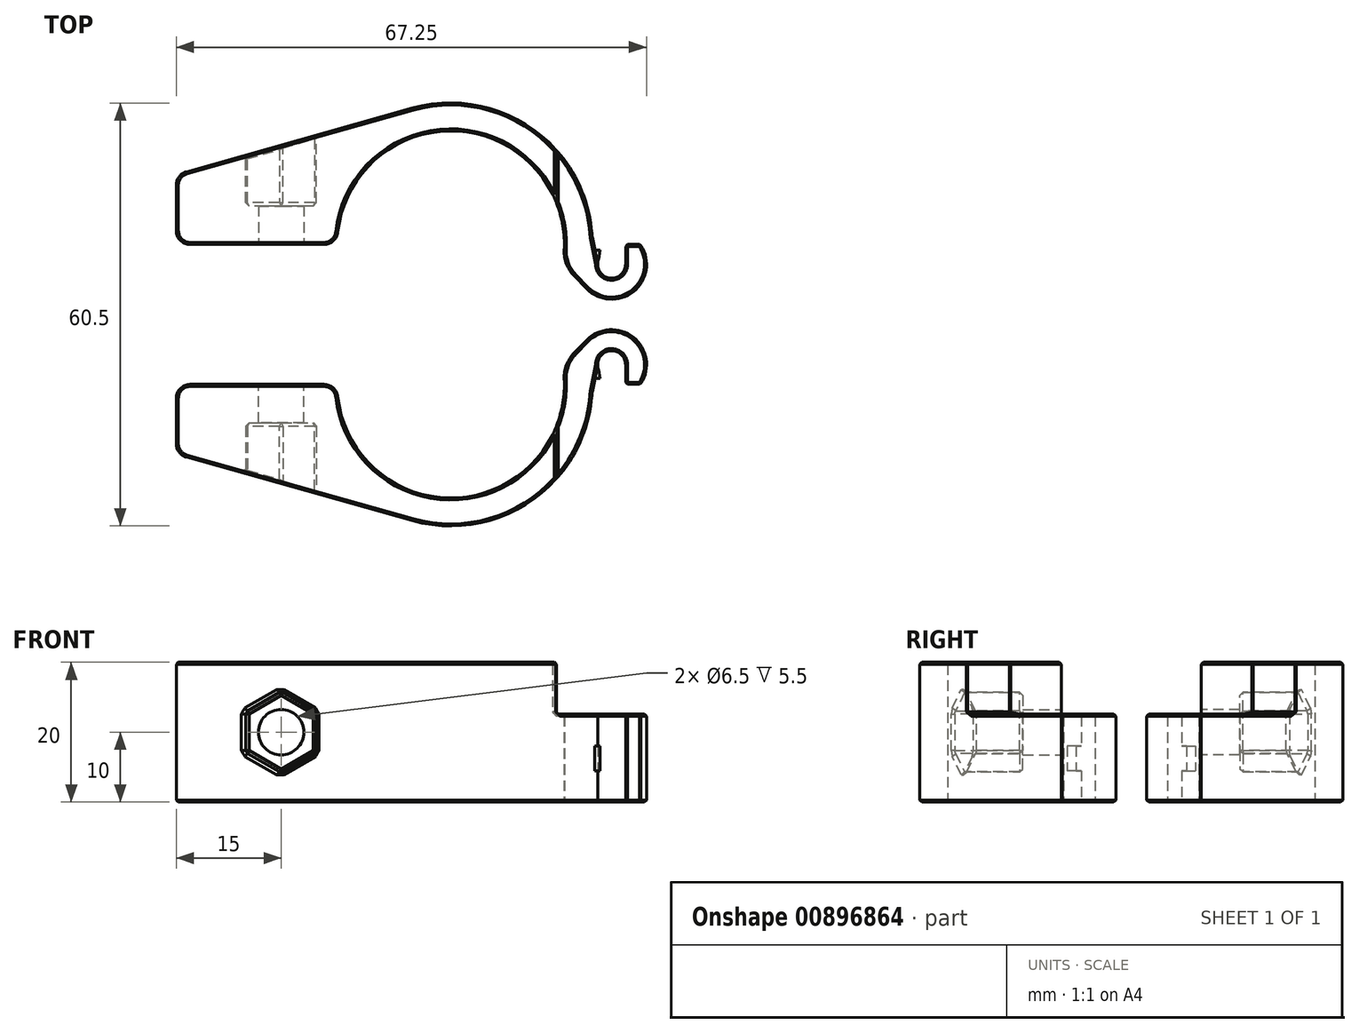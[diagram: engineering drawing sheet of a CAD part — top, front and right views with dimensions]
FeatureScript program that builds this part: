
annotation { "Feature Type Name" : "Feature", "Feature Type Description" : "" }
export const myFeature = defineFeature(function(context is Context, id is Id, definition is map)
    precondition{}
    {
        {
            var Q0;
            Q0=qCreatedBy(makeId("Top.planeOp"),FACE);
            var sketch = newSketch(context, id + "F0", { "sketchPlane" : qUnion([Q0])});
            skLineSegment(sketch, "E0", {"start": v(0, 0) * mm, "end": v(-16.25, 0) * mm, "construction": true});
            skLineSegment(sketch, "E1", {"start": v(0, 0) * mm, "end": v(16.25, 0) * mm, "construction": true});
            skLineSegment(sketch, "E2", {"start": v(0, 0) * mm, "end": v(16, -2.82) * mm, "construction": true});
            skArc(sketch, "E3", {"start": v(-16.25, 0) * mm, "mid": v(-1.42, -16.19) * mm, "end": v(16, -2.82) * mm, "construction": true});
            skArc(sketch, "E4", {"start": v(16, -2.82) * mm, "mid": v(1.42, 16.19) * mm, "end": v(-16.25, 0) * mm});
            skArc(sketch, "E5.0", {"start": v(19.94, -3.52) * mm, "mid": v(20.22, -1.1) * mm, "end": v(20.2, 1.32) * mm, "construction": true});
            skLineSegment(sketch, "E6", {"start": v(16, -2.82) * mm, "end": v(19.94, -3.52) * mm, "construction": true});
            skLineSegment(sketch, "E7", {"start": v(-16.25, 0) * mm, "end": v(-39.25, 0) * mm});
            skLineSegment(sketch, "E8", {"start": v(-39.25, 0) * mm, "end": v(-39.25, 10) * mm});
            skLineSegment(sketch, "E9", {"start": v(-39.25, 10) * mm, "end": v(-5.48, 19.5) * mm});
            skArc(sketch, "E10", {"start": v(-5.48, 19.5) * mm, "mid": v(-16.14, 12.23) * mm, "end": v(-20.25, 0) * mm, "construction": true});
            skArc(sketch, "E11", {"start": v(20.2, 1.32) * mm, "mid": v(11.7, 16.53) * mm, "end": v(-5.48, 19.5) * mm});
            skArc(sketch, "E12", {"start": v(20.2, 1.32) * mm, "mid": v(18.5, -0.63) * mm, "end": v(18.02, -3.18) * mm, "construction": true});
            skArc(sketch, "E13", {"start": v(18.02, -3.18) * mm, "mid": v(24.65, -7.54) * mm, "end": v(27.13, 0) * mm});
            skLineSegment(sketch, "E14", {"start": v(16, -2.82) * mm, "end": v(19.43, -6.32) * mm});
            skLineSegment(sketch, "E15", {"start": v(23, -2.82) * mm, "end": v(25, -2.82) * mm, "construction": true});
            skLineSegment(sketch, "E16", {"start": v(25, -2.82) * mm, "end": v(25, 0) * mm});
            skLineSegment(sketch, "E17", {"start": v(27.13, 0) * mm, "end": v(25, 0) * mm});
            skLineSegment(sketch, "E18", {"start": v(25, 0) * mm, "end": v(25, 1.76) * mm, "construction": true});
            skLineSegment(sketch, "E19", {"start": v(23, -2.82) * mm, "end": v(21, -2.82) * mm, "construction": true});
            skLineSegment(sketch, "E20", {"start": v(21, -2.82) * mm, "end": v(21, -2.82) * mm});
            skArc(sketch, "E21", {"start": v(27.13, 0) * mm, "mid": v(23.94, 2.09) * mm, "end": v(20.2, 1.32) * mm, "construction": true});
            skLineSegment(sketch, "E22", {"start": v(21, -2.82) * mm, "end": v(20.2, 1.32) * mm});
            skArc(sketch, "E23", {"start": v(21, -2.82) * mm, "mid": v(23, -4.82) * mm, "end": v(25, -2.82) * mm});
            skArc(sketch, "E24", {"start": v(25, -2.82) * mm, "mid": v(23, -0.82) * mm, "end": v(21, -2.82) * mm});
            skLineSegment(sketch, "E25", {"start": v(21, -2.82) * mm, "end": v(21, -0.82) * mm, "construction": true});
            skLineSegment(sketch, "E26", {"start": v(21, -2.82) * mm, "end": v(21.38, -0.82) * mm});
            skLineSegment(sketch, "E27", {"start": v(21.38, -0.82) * mm, "end": v(20.62, -0.82) * mm});
            skSolve(sketch);
        }
        {
            var Q0;
            Q0=makeQuery(id+"F0.imprint","IMPRINT",FACE,{"disambiguationData":[TD([[makeQuery(id+"F0.imprint","IMPRINT",EDGE,{"derivedFrom":sQuery(id+"F0.wireOp",EDGE,"E4")}),-1.0]])]});
            extrude(context, id + "F1", {"entities" : qUnion([Q0]), "depth" : 12.6 * mm, "offsetDistance" : 25 * mm});
        }
        {
            var Q0;
            Q0=makeQuery(id+"F1.opExtrude","CAP_FACE",FACE,{"disambiguationData":[OSD([sQuery(id+"F0.wireOp",EDGE,"E4"),sQuery(id+"F0.wireOp",EDGE,"E7"),sQuery(id+"F0.wireOp",EDGE,"E8"),sQuery(id+"F0.wireOp",EDGE,"E9"),sQuery(id+"F0.wireOp",EDGE,"E11"),sQuery(id+"F0.wireOp",EDGE,"E13"),sQuery(id+"F0.wireOp",EDGE,"E14"),sQuery(id+"F0.wireOp",EDGE,"E16"),sQuery(id+"F0.wireOp",EDGE,"E17"),sQuery(id+"F0.wireOp",EDGE,"E22"),sQuery(id+"F0.wireOp",EDGE,"E23")])],"isStart":false});
            var sketch = newSketch(context, id + "F2", { "sketchPlane" : qUnion([Q0])});
            skPoint(sketch, "E28.0", {"position": v(16.25, 0) * mm});
            skLineSegment(sketch, "E29", {"start": v(16.25, 0) * mm, "end": v(16.25, 6) * mm, "construction": true});
            skLineSegment(sketch, "E30", {"start": v(16.25, 6) * mm, "end": v(15.1, 6) * mm, "construction": true});
            skLineSegment(sketch, "E31", {"start": v(15.1, 6) * mm, "end": v(15.1, 13.5) * mm});
            skSolve(sketch);
        }
        {
            var Q0;
            {var subQ3=sQuery(id+"F2.wireOp",EDGE,"E31");Q0=makeQuery(id+"F2.imprint","IMPRINT",FACE,{"disambiguationData":[TD([[makeQuery(id+"F2.imprint","IMPRINT",EDGE,{"derivedFrom":subQ3}),1.0]])]});}
            extrude(context, id + "F3", {"entities" : qUnion([Q0]), "operationType" : NewBodyOperationType.ADD, "depth" : (20 - 12.6) * mm, "offsetDistance" : 25 * mm});
        }
        {
            var Q0;
            {var subQ0=sQuery(id+"F0.wireOp",EDGE,"E7");Q0=makeQuery(id+"F3.boolean.opBoolean","MERGE",FACE,{"derivedFrom":[makeQuery(id+"F1.opExtrude","SWEPT_FACE",FACE,{"disambiguationData":[OSD([subQ0])]}),makeQuery(id+"F3.opExtrude","SWEPT_FACE",FACE,{"disambiguationData":[OSD([subQ0])]})]});}
            var sketch = newSketch(context, id + "F4", { "sketchPlane" : qUnion([Q0])});
            skLineSegment(sketch, "E32", {"start": v(-39.25, 0) * mm, "end": v(-16.25, 20) * mm, "construction": true});
            skLineSegment(sketch, "E33", {"start": v(-16.25, 0) * mm, "end": v(-39.25, 20) * mm, "construction": true});
            skPoint(sketch, "E34", {"position": v(-24.25, 10) * mm});
            skCircle(sketch, "E35", {"center": v(-24.25, 10) * mm, "radius": 3.25 * mm});
            skCircle(sketch, "E36.cCircle", {"center": v(-24.25, 10) * mm, "radius": 5.05 * mm, "construction": true});
            skLineSegment(sketch, "E36.0", {"start": v(-19.2, 12.92) * mm, "end": v(-19.2, 7.08) * mm});
            skLineSegment(sketch, "E36.1", {"start": v(-19.2, 7.08) * mm, "end": v(-24.25, 4.17) * mm});
            skLineSegment(sketch, "E36.2", {"start": v(-24.25, 4.17) * mm, "end": v(-29.3, 7.08) * mm});
            skLineSegment(sketch, "E36.3", {"start": v(-29.3, 7.08) * mm, "end": v(-29.3, 12.92) * mm});
            skLineSegment(sketch, "E36.4", {"start": v(-29.3, 12.92) * mm, "end": v(-24.25, 15.83) * mm});
            skLineSegment(sketch, "E36.5", {"start": v(-24.25, 15.83) * mm, "end": v(-19.2, 12.92) * mm});
            skPoint(sketch, "E36.0.midPoint", {"position": v(-19.2, 10) * mm});
            skLineSegment(sketch, "E37", {"start": v(-39.25, 10) * mm, "end": v(-16.25, 10) * mm, "construction": true});
            skLineSegment(sketch, "E38", {"start": v(-27.75, 0) * mm, "end": v(-27.75, 20) * mm, "construction": true});
            skSolve(sketch);
        }
        {
            var Q0;
            Q0=makeQuery(id+"F4.imprint","IMPRINT",FACE,{"disambiguationData":[TD([[makeQuery(id+"F4.imprint","IMPRINT",EDGE,{"derivedFrom":sQuery(id+"F4.wireOp",EDGE,"E35")}),1.0]])]});
            extrude(context, id + "F5", {"entities" : qUnion([Q0]), "operationType" : NewBodyOperationType.REMOVE, "endBound" : BoundingType.THROUGH_ALL, "oppositeDirection" : true, "depth" : 25 * mm, "offsetDistance" : 25 * mm});
        }
        {
            var Q0;
            Q0=makeQuery(id+"F4.imprint","IMPRINT",FACE,{"disambiguationData":[TD([[makeQuery(id+"F4.imprint","IMPRINT",EDGE,{"derivedFrom":sQuery(id+"F4.wireOp",EDGE,"E35")}),-1.0]])]});
            extrude(context, id + "F6", {"entities" : qUnion([Q0]), "operationType" : NewBodyOperationType.REMOVE, "endBound" : BoundingType.THROUGH_ALL, "oppositeDirection" : true, "depth" : 25 * mm, "offsetDistance" : 25 * mm, "hasSecondDirection" : true, "secondDirectionOppositeDirection" : false, "secondDirectionDepth" : -5.5 * mm});
        }
        {
            var Q0;
            {var subQ4=sQuery(id+"F0.wireOp",EDGE,"E27");Q0=makeQuery(id+"F0.imprint","IMPRINT",FACE,{"disambiguationData":[TD([[makeQuery(id+"F0.imprint","IMPRINT",EDGE,{"derivedFrom":subQ4}),1.0]])]});}
            extrude(context, id + "F7", {"entities" : qUnion([Q0]), "operationType" : NewBodyOperationType.ADD, "depth" : 8 * mm, "offsetDistance" : 25 * mm, "hasSecondDirection" : true, "secondDirectionOppositeDirection" : true, "secondDirectionDepth" : -4.5 * mm});
        }
        {
            var Q0;
            {var subQ0=sQuery(id+"F0.wireOp",EDGE,"E7");var subQ1=sQuery(id+"F0.wireOp",EDGE,"E4");Q0=makeQuery(id+"F3.boolean.opBoolean","MERGE",EDGE,{"derivedFrom":[makeQuery(id+"F1.opExtrude","SWEPT_EDGE",EDGE,{"disambiguationData":[OSD([subQ1,subQ0])]}),makeQuery(id+"F3.opExtrude","SWEPT_EDGE",EDGE,{"disambiguationData":[OSD([subQ1,subQ0])]})]});}
            var Q1;
            {var subQ0=sQuery(id+"F0.wireOp",EDGE,"E8");var subQ1=sQuery(id+"F0.wireOp",EDGE,"E7");Q1=makeQuery(id+"F3.boolean.opBoolean","MERGE",EDGE,{"derivedFrom":[makeQuery(id+"F1.opExtrude","SWEPT_EDGE",EDGE,{"disambiguationData":[OSD([subQ1,subQ0])]}),makeQuery(id+"F3.opExtrude","SWEPT_EDGE",EDGE,{"disambiguationData":[OSD([subQ1,subQ0])]})]});}
            var Q2;
            {var subQ0=sQuery(id+"F0.wireOp",EDGE,"E9");var subQ1=sQuery(id+"F0.wireOp",EDGE,"E8");Q2=makeQuery(id+"F3.boolean.opBoolean","MERGE",EDGE,{"derivedFrom":[makeQuery(id+"F1.opExtrude","SWEPT_EDGE",EDGE,{"disambiguationData":[OSD([subQ1,subQ0])]}),makeQuery(id+"F3.opExtrude","SWEPT_EDGE",EDGE,{"disambiguationData":[OSD([subQ1,subQ0])]})]});}
            fillet(context, id + "F8", {"entities" : qUnion([Q0, Q1, Q2]), "radius" : 2 * mm, "tangentPropagation" : true, "allowEdgeOverflow" : false});
        }
        {
            var Q0;
            Q0=makeQuery(id+"F1.opExtrude","SWEPT_EDGE",EDGE,{"disambiguationData":[OSD([sQuery(id+"F0.wireOp",EDGE,"E4"),sQuery(id+"F0.wireOp",EDGE,"E14")])]});
            var Q1;
            Q1=makeQuery(id+"F1.opExtrude","SWEPT_EDGE",EDGE,{"disambiguationData":[OSD([sQuery(id+"F0.wireOp",EDGE,"E13"),sQuery(id+"F0.wireOp",EDGE,"E14")])]});
            var Q2;
            Q2=makeQuery(id+"F1.opExtrude","SWEPT_EDGE",EDGE,{"disambiguationData":[OSD([sQuery(id+"F0.wireOp",EDGE,"E11"),sQuery(id+"F0.wireOp",EDGE,"E22")])]});
            fillet(context, id + "F9", {"entities" : qUnion([Q0, Q1, Q2]), "radius" : 5 * mm, "tangentPropagation" : true, "allowEdgeOverflow" : false});
        }
        {
            var Q0;
            Q0=makeQuery(id+"F3.opExtrude","CAP_FACE",FACE,{"disambiguationData":[OSD([sQuery(id+"F0.wireOp",EDGE,"E4"),sQuery(id+"F0.wireOp",EDGE,"E7"),sQuery(id+"F0.wireOp",EDGE,"E8"),sQuery(id+"F0.wireOp",EDGE,"E9"),sQuery(id+"F0.wireOp",EDGE,"E11"),sQuery(id+"F2.wireOp",EDGE,"E31")])],"isStart":false});
            var Q1;
            Q1=makeQuery(id+"F1.opExtrude","CAP_FACE",FACE,{"disambiguationData":[OSD([sQuery(id+"F0.wireOp",EDGE,"E4"),sQuery(id+"F0.wireOp",EDGE,"E7"),sQuery(id+"F0.wireOp",EDGE,"E8"),sQuery(id+"F0.wireOp",EDGE,"E9"),sQuery(id+"F0.wireOp",EDGE,"E11"),sQuery(id+"F0.wireOp",EDGE,"E13"),sQuery(id+"F0.wireOp",EDGE,"E14"),sQuery(id+"F0.wireOp",EDGE,"E16"),sQuery(id+"F0.wireOp",EDGE,"E17"),sQuery(id+"F0.wireOp",EDGE,"E22"),sQuery(id+"F0.wireOp",EDGE,"E23")])],"isStart":true});
            var Q2;
            Q2=makeQuery(id+"F1.opExtrude","CAP_FACE",FACE,{"disambiguationData":[OSD([sQuery(id+"F0.wireOp",EDGE,"E4"),sQuery(id+"F0.wireOp",EDGE,"E7"),sQuery(id+"F0.wireOp",EDGE,"E8"),sQuery(id+"F0.wireOp",EDGE,"E9"),sQuery(id+"F0.wireOp",EDGE,"E11"),sQuery(id+"F0.wireOp",EDGE,"E13"),sQuery(id+"F0.wireOp",EDGE,"E14"),sQuery(id+"F0.wireOp",EDGE,"E16"),sQuery(id+"F0.wireOp",EDGE,"E17"),sQuery(id+"F0.wireOp",EDGE,"E22"),sQuery(id+"F0.wireOp",EDGE,"E23")])],"isStart":false});
            var Q3;
            Q3=makeQuery(id+"F1.opExtrude","SWEPT_EDGE",EDGE,{"disambiguationData":[OSD([sQuery(id+"F0.wireOp",EDGE,"E13"),sQuery(id+"F0.wireOp",EDGE,"E17")])]});
            var Q4;
            Q4=makeQuery(id+"F1.opExtrude","SWEPT_EDGE",EDGE,{"disambiguationData":[OSD([sQuery(id+"F0.wireOp",EDGE,"E16"),sQuery(id+"F0.wireOp",EDGE,"E17")])]});
            chamfer(context, id + "F10", {"entities" : qUnion([Q0, Q1, Q2, Q3, Q4]), "width" : 0.3 * mm, "tangentPropagation" : true});
        }
        {
            var Q0;
            Q0=makeQuery(id+"F5.boolean.opBoolean","COPY",EDGE,{"derivedFrom":makeQuery(id+"F5.opExtrude","CAP_EDGE",EDGE,{"disambiguationData":[OSD([sQuery(id+"F4.wireOp",EDGE,"E35")])],"isStart":true})});
            var Q1;
            Q1=makeQuery(id+"F6.boolean.opBoolean","COPY",FACE,{"derivedFrom":makeQuery(id+"F6.opExtrude","SWEPT_FACE",FACE,{"disambiguationData":[OSD([sQuery(id+"F4.wireOp",EDGE,"E36.0")])]})});
            var Q2;
            Q2=makeQuery(id+"F6.boolean.opBoolean","COPY",FACE,{"derivedFrom":makeQuery(id+"F6.opExtrude","SWEPT_FACE",FACE,{"disambiguationData":[OSD([sQuery(id+"F4.wireOp",EDGE,"E36.4")])]})});
            var Q3;
            Q3=makeQuery(id+"F6.boolean.opBoolean","COPY",FACE,{"derivedFrom":makeQuery(id+"F6.opExtrude","SWEPT_FACE",FACE,{"disambiguationData":[OSD([sQuery(id+"F4.wireOp",EDGE,"E36.2")])]})});
            var Q4;
            Q4=makeQuery(id+"F6.boolean.opBoolean","COPY",FACE,{"derivedFrom":makeQuery(id+"F6.opExtrude","SWEPT_FACE",FACE,{"disambiguationData":[OSD([sQuery(id+"F4.wireOp",EDGE,"E36.1")])]})});
            var Q5;
            Q5=makeQuery(id+"F6.boolean.opBoolean","COPY",FACE,{"derivedFrom":makeQuery(id+"F6.opExtrude","SWEPT_FACE",FACE,{"disambiguationData":[OSD([sQuery(id+"F4.wireOp",EDGE,"E36.5")])]})});
            var Q6;
            Q6=makeQuery(id+"F6.boolean.opBoolean","COPY",FACE,{"derivedFrom":makeQuery(id+"F6.opExtrude","SWEPT_FACE",FACE,{"disambiguationData":[OSD([sQuery(id+"F4.wireOp",EDGE,"E36.3")])]})});
            var Q7;
            Q7=makeQuery(id+"F6.boolean.opBoolean","COPY",EDGE,{"derivedFrom":makeQuery(id+"F6.opExtrude","CAP_EDGE",EDGE,{"disambiguationData":[OSD([sQuery(id+"F4.wireOp",EDGE,"E35")])],"isStart":true})});
            chamfer(context, id + "F11", {"entities" : qUnion([Q0, Q1, Q2, Q3, Q4, Q5, Q6, Q7]), "width" : 0.5 * mm, "tangentPropagation" : true});
        }
        {
            var Q0;
            {var subQ0=sQuery(id+"F0.wireOp",EDGE,"E7");Q0=makeQuery(id+"F3.boolean.opBoolean","MERGE",FACE,{"derivedFrom":[makeQuery(id+"F1.opExtrude","SWEPT_FACE",FACE,{"disambiguationData":[OSD([subQ0])]}),makeQuery(id+"F3.opExtrude","SWEPT_FACE",FACE,{"disambiguationData":[OSD([subQ0])]})]});}
            cPlane(context, id + "F12", {"entities" : qUnion([Q0]), "cplaneType" : CPlaneType.OFFSET, "offset" : 10 * mm, "width" : 150 * mm, "height" : 150 * mm});
        }
        {
            var Q0;
            Q0=makeQuery(id+"F1.opExtrude","SWEPT_BODY",BODY,{"disambiguationData":[OSD([sQuery(id+"F0.wireOp",EDGE,"E4"),sQuery(id+"F0.wireOp",EDGE,"E7"),sQuery(id+"F0.wireOp",EDGE,"E8"),sQuery(id+"F0.wireOp",EDGE,"E9"),sQuery(id+"F0.wireOp",EDGE,"E11"),sQuery(id+"F0.wireOp",EDGE,"E13"),sQuery(id+"F0.wireOp",EDGE,"E14"),sQuery(id+"F0.wireOp",EDGE,"E16"),sQuery(id+"F0.wireOp",EDGE,"E17"),sQuery(id+"F0.wireOp",EDGE,"E22"),sQuery(id+"F0.wireOp",EDGE,"E23")])]});
            var Q1;
            Q1=qCreatedBy(id+"F12.planeOp",FACE);
            mirror(context, id + "F13", {"entities" : qUnion([Q0]), "mirrorPlane" : qUnion([Q1])});
        }
    });
